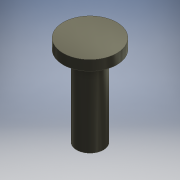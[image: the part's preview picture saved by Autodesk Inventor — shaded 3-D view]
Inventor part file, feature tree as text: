
AUTODESK INVENTOR PART (.ipt)
format: ipt  version: 2016 (Build 200138000, 138)  size: 96,256 bytes
history: native  units: mm
features: extrude x2, other x1, sketch x1
ambient origin geometry x8: Origin, YZ Plane, XZ Plane, XY Plane, X Axis, Y Axis, Z Axis, Center Point
bodies: Body1 (feature_tree)
feature tree (4):
  other  "ソリッド1"
  sketch  "スケッチ1"
  extrude  "押し出し1"  Depth=8.0mm
  extrude  "押し出し2"  Depth=4.0mm
